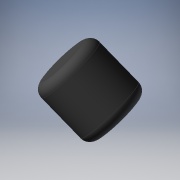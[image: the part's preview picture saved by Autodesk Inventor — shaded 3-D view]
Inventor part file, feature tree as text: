
AUTODESK INVENTOR PART (.ipt)
format: ipt  version: 2019 (Build 230136000, 136)  size: 148,992 bytes
history: native  units: mm
features: revolve x1, sketch x1
ambient origin geometry x8: Origin, YZ Plane, XZ Plane, XY Plane, X Axis, Y Axis, Z Axis, Center Point
bodies: Solid1 (feature_tree)
feature tree (2):
  revolve  "Revolution1"  [1 undecoded]
  sketch  "Sketch_1"  dims[d0=360.0deg]
note: 1 required parameter value undecoded (feature->parameter linkage not recoverable at this tier; creation-order binding heuristic only, values carry confidence <= 0.55)
